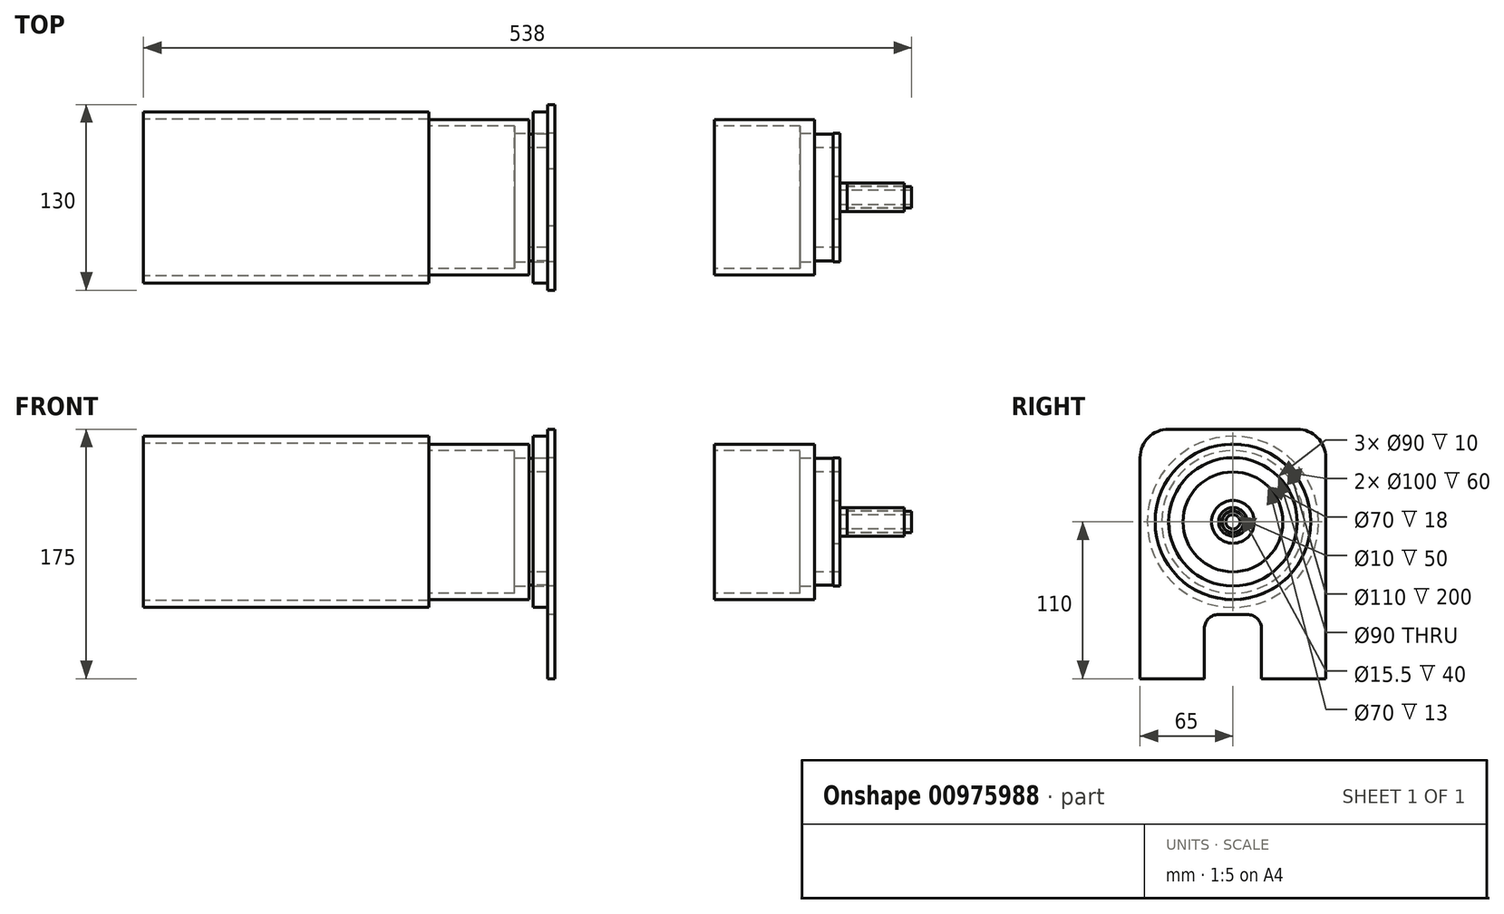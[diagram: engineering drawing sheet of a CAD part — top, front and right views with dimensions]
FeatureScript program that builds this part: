
annotation { "Feature Type Name" : "Feature", "Feature Type Description" : "" }
export const myFeature = defineFeature(function(context is Context, id is Id, definition is map)
    precondition{}
    {
        {
            var Q0;
            Q0=qCreatedBy(makeId("Right.planeOp"),FACE);
            var sketch = newSketch(context, id + "F0", { "sketchPlane" : qUnion([Q0])});
            skCircle(sketch, "E0", {"center": v(0, 0) * mm, "radius": 60 * mm});
            skCircle(sketch, "E1", {"center": v(0, 0) * mm, "radius": 55 * mm});
            skSolve(sketch);
        }
        {
            var Q0;
            Q0 = qSketchRegion(id + "F0", true);
            extrude(context, id + "F1", {"entities" : qUnion([Q0]), "depth" : 200 * mm, "offsetDistance" : 25 * mm});
        }
        {
            var Q0;
            Q0=makeQuery(id+"F1.opExtrude","CAP_FACE",FACE,{"disambiguationData":[OSD([sQuery(id+"F0.wireOp",EDGE,"E0"),sQuery(id+"F0.wireOp",EDGE,"E1")])],"isStart":false});
            var sketch = newSketch(context, id + "F2", { "sketchPlane" : qUnion([Q0])});
            skCircle(sketch, "E2", {"center": v(0, 0) * mm, "radius": 54.5 * mm});
            skCircle(sketch, "E3", {"center": v(0, 0) * mm, "radius": 50 * mm});
            skSolve(sketch);
        }
        {
            var Q0;
            Q0 = qSketchRegion(id + "F2", true);
            extrude(context, id + "F3", {"entities" : qUnion([Q0]), "depth" : 70 * mm, "offsetDistance" : 25 * mm});
        }
        {
            var Q0;
            Q0=makeQuery(id+"F3.opExtrude","CAP_FACE",FACE,{"disambiguationData":[OSD([sQuery(id+"F2.wireOp",EDGE,"E2"),sQuery(id+"F2.wireOp",EDGE,"E3")])],"isStart":false});
            var sketch = newSketch(context, id + "F4", { "sketchPlane" : qUnion([Q0])});
            skCircle(sketch, "E4", {"center": v(0, 0) * mm, "radius": 50.5 * mm});
            skCircle(sketch, "E5", {"center": v(0, 0) * mm, "radius": 45 * mm});
            skSolve(sketch);
        }
        {
            var Q0;
            Q0=makeQuery(id+"F4.imprint","IMPRINT",FACE,{"disambiguationData":[TD([[makeQuery(id+"F4.imprint","IMPRINT",EDGE,{"derivedFrom":sQuery(id+"F4.wireOp",EDGE,"E5")}),-1.0]])]});
            extrude(context, id + "F5", {"entities" : qUnion([Q0]), "operationType" : NewBodyOperationType.ADD, "oppositeDirection" : true, "depth" : 10 * mm, "offsetDistance" : 25 * mm});
        }
        {
            var Q0;
            {var subQ0=sQuery(id+"F2.wireOp",EDGE,"E3");Q0=makeQuery(id+"F5.boolean.opBoolean","MERGE",FACE,{"derivedFrom":[makeQuery(id+"F3.opExtrude","CAP_FACE",FACE,{"disambiguationData":[OSD([sQuery(id+"F2.wireOp",EDGE,"E2"),subQ0])],"isStart":false}),makeQuery(id+"F5.opExtrude","CAP_FACE",FACE,{"disambiguationData":[OSD([subQ0,sQuery(id+"F4.wireOp",EDGE,"E5")])],"isStart":true})]});}
            var sketch = newSketch(context, id + "F6", { "sketchPlane" : qUnion([Q0])});
            skCircle(sketch, "E6", {"center": v(0, 0) * mm, "radius": 44.5 * mm});
            skCircle(sketch, "E7", {"center": v(0, 0) * mm, "radius": 35 * mm});
            skSolve(sketch);
        }
        {
            var Q0;
            Q0=makeQuery(id+"F6.imprint","IMPRINT",FACE,{"disambiguationData":[TD([[makeQuery(id+"F6.imprint","IMPRINT",EDGE,{"derivedFrom":sQuery(id+"F6.wireOp",EDGE,"E6")}),1.0]])]});
            extrude(context, id + "F7", {"entities" : qUnion([Q0]), "depth" : 13 * mm, "offsetDistance" : 25 * mm});
        }
        {
            var Q0;
            Q0=makeQuery(id+"F7.opExtrude","CAP_FACE",FACE,{"disambiguationData":[OSD([sQuery(id+"F6.wireOp",EDGE,"E6"),sQuery(id+"F6.wireOp",EDGE,"E7")])],"isStart":false});
            var sketch = newSketch(context, id + "F8", { "sketchPlane" : qUnion([Q0])});
            skCircle(sketch, "E8", {"center": v(0, 0) * mm, "radius": 45 * mm});
            skCircle(sketch, "E9", {"center": v(0, 0) * mm, "radius": 60 * mm});
            skSolve(sketch);
        }
        {
            var Q0;
            Q0=makeQuery(id+"F8.imprint","IMPRINT",FACE,{"disambiguationData":[TD([[makeQuery(id+"F8.imprint","IMPRINT",EDGE,{"derivedFrom":sQuery(id+"F8.wireOp",EDGE,"E8")}),-1.0]])]});
            extrude(context, id + "F9", {"entities" : qUnion([Q0]), "oppositeDirection" : true, "depth" : 10 * mm, "offsetDistance" : 25 * mm});
        }
        {
            var Q0;
            Q0=makeQuery(id+"F9.opExtrude","CAP_FACE",FACE,{"disambiguationData":[OSD([sQuery(id+"F8.wireOp",EDGE,"E8"),sQuery(id+"F8.wireOp",EDGE,"E9")])],"isStart":true});
            var sketch = newSketch(context, id + "F10", { "sketchPlane" : qUnion([Q0])});
            skCircle(sketch, "E10", {"center": v(0, 0) * mm, "radius": 45 * mm});
            skLineSegment(sketch, "E11.bottom", {"start": v(-65, 65) * mm, "end": v(65, 65) * mm});
            skLineSegment(sketch, "E11.top", {"start": v(-65, -65) * mm, "end": v(65, -65) * mm});
            skLineSegment(sketch, "E11.left", {"start": v(-65, 65) * mm, "end": v(-65, -65) * mm});
            skLineSegment(sketch, "E11.right", {"start": v(65, 65) * mm, "end": v(65, -65) * mm});
            skLineSegment(sketch, "E12", {"start": v(65, 0) * mm, "end": v(-65, 0) * mm, "construction": true});
            skLineSegment(sketch, "E13.bottom", {"start": v(-65, -65) * mm, "end": v(-20, -65) * mm});
            skLineSegment(sketch, "E13.top", {"start": v(-65, -110) * mm, "end": v(-20, -110) * mm});
            skLineSegment(sketch, "E13.left", {"start": v(-65, -65) * mm, "end": v(-65, -110) * mm});
            skLineSegment(sketch, "E13.right", {"start": v(-20, -65) * mm, "end": v(-20, -110) * mm});
            skLineSegment(sketch, "E14.bottom", {"start": v(65, -65) * mm, "end": v(20, -65) * mm});
            skLineSegment(sketch, "E14.top", {"start": v(65, -110) * mm, "end": v(20, -110) * mm});
            skLineSegment(sketch, "E14.left", {"start": v(65, -65) * mm, "end": v(65, -110) * mm});
            skLineSegment(sketch, "E14.right", {"start": v(20, -65) * mm, "end": v(20, -110) * mm});
            skSolve(sketch);
        }
        {
            var Q0;
            Q0 = qSketchRegion(id + "F10", true);
            extrude(context, id + "F11", {"entities" : qUnion([Q0]), "depth" : 5 * mm, "offsetDistance" : 25 * mm});
        }
        {
            var Q0;
            Q0=makeQuery(id+"F11.opExtrude","SWEPT_EDGE",EDGE,{"disambiguationData":[OSD([sQuery(id+"F10.wireOp",EDGE,"E11.bottom"),sQuery(id+"F10.wireOp",EDGE,"E11.left")])]});
            var Q1;
            Q1=makeQuery(id+"F11.opExtrude","SWEPT_EDGE",EDGE,{"disambiguationData":[OSD([sQuery(id+"F10.wireOp",EDGE,"E11.bottom"),sQuery(id+"F10.wireOp",EDGE,"E11.right")])]});
            fillet(context, id + "F12", {"entities" : qUnion([Q0, Q1]), "radius" : 20 * mm, "tangentPropagation" : true, "allowEdgeOverflow" : false});
        }
        {
            var Q0;
            Q0=makeQuery(id+"F11.opExtrude","SWEPT_EDGE",EDGE,{"disambiguationData":[OSD([sQuery(id+"F10.wireOp",EDGE,"E11.top"),sQuery(id+"F10.wireOp",EDGE,"E13.bottom"),sQuery(id+"F10.wireOp",EDGE,"E13.right")])]});
            var Q1;
            Q1=makeQuery(id+"F11.opExtrude","SWEPT_EDGE",EDGE,{"disambiguationData":[OSD([sQuery(id+"F10.wireOp",EDGE,"E11.top"),sQuery(id+"F10.wireOp",EDGE,"E14.bottom"),sQuery(id+"F10.wireOp",EDGE,"E14.right")])]});
            fillet(context, id + "F13", {"entities" : qUnion([Q0, Q1]), "radius" : 10 * mm, "tangentPropagation" : true, "allowEdgeOverflow" : false});
        }
        {
            var Q0;
            Q0=makeQuery(id+"F3.opExtrude","SWEPT_BODY",BODY,{"disambiguationData":[OSD([sQuery(id+"F2.wireOp",EDGE,"E2"),sQuery(id+"F2.wireOp",EDGE,"E3")])]});
            transform(context, id + "F14", {"entities" : qUnion([Q0]), "transformType" : TransformType.TRANSLATION_3D, "dx" : 200 * mm, "dy" : 0 * mm, "dz" : 0 * mm, "makeCopy" : true});
        }
        {
            var Q0;
            Q0=makeQuery(id+"F7.opExtrude","SWEPT_BODY",BODY,{"disambiguationData":[OSD([sQuery(id+"F6.wireOp",EDGE,"E6"),sQuery(id+"F6.wireOp",EDGE,"E7")])]});
            transform(context, id + "F15", {"entities" : qUnion([Q0]), "transformType" : TransformType.TRANSLATION_3D, "dx" : 200 * mm, "dy" : 0 * mm, "dz" : 0 * mm, "makeCopy" : true});
        }
        {
            var Q0;
            Q0=makeQuery(id+"F15.opPattern","COPY",FACE,{"derivedFrom":makeQuery(id+"F7.opExtrude","CAP_FACE",FACE,{"disambiguationData":[OSD([sQuery(id+"F6.wireOp",EDGE,"E6"),sQuery(id+"F6.wireOp",EDGE,"E7")])],"isStart":false}),"instanceName":"1"});
            var sketch = newSketch(context, id + "F16", { "sketchPlane" : qUnion([Q0])});
            skCircle(sketch, "E15", {"center": v(0, 0) * mm, "radius": 35 * mm});
            skCircle(sketch, "E16", {"center": v(0, 0) * mm, "radius": 32.5 * mm});
            skSolve(sketch);
        }
        {
            var Q0;
            Q0 = qSketchRegion(id + "F16", true);
            extrude(context, id + "F17", {"entities" : qUnion([Q0]), "oppositeDirection" : true, "depth" : 5 * mm, "offsetDistance" : 25 * mm});
        }
        {
            var Q0;
            Q0=makeQuery(id+"F17.opExtrude","CAP_FACE",FACE,{"disambiguationData":[OSD([sQuery(id+"F16.wireOp",EDGE,"E15"),sQuery(id+"F16.wireOp",EDGE,"E16")])],"isStart":true});
            var sketch = newSketch(context, id + "F18", { "sketchPlane" : qUnion([Q0])});
            skCircle(sketch, "E17", {"center": v(0, 0) * mm, "radius": 45 * mm});
            skSolve(sketch);
        }
        {
            var Q0;
            Q0 = qSketchRegion(id + "F18", true);
            extrude(context, id + "F19", {"entities" : qUnion([Q0]), "operationType" : NewBodyOperationType.ADD, "depth" : 5 * mm, "offsetDistance" : 25 * mm});
        }
        {
            var Q0;
            Q0=makeQuery(id+"F19.opExtrude","CAP_FACE",FACE,{"disambiguationData":[OSD([sQuery(id+"F18.wireOp",EDGE,"E17")])],"isStart":false});
            var sketch = newSketch(context, id + "F20", { "sketchPlane" : qUnion([Q0])});
            skCircle(sketch, "E18", {"center": v(0, 0) * mm, "radius": 35 * mm});
            skCircle(sketch, "E19", {"center": v(0, 0) * mm, "radius": 15 * mm});
            skSolve(sketch);
        }
        {
            var Q0;
            Q0=makeQuery(id+"F20.imprint","IMPRINT",FACE,{"disambiguationData":[TD([[makeQuery(id+"F20.imprint","IMPRINT",EDGE,{"derivedFrom":sQuery(id+"F20.wireOp",EDGE,"E18")}),1.0]])]});
            extrude(context, id + "F21", {"entities" : qUnion([Q0]), "operationType" : NewBodyOperationType.REMOVE, "endBound" : BoundingType.UP_TO_NEXT, "oppositeDirection" : true, "depth" : 25 * mm, "offsetDistance" : 25 * mm});
        }
        {
            var Q0;
            Q0=makeQuery(id+"F21.boolean.opBoolean","SPLIT",FACE,{"disambiguationData":[TD([makeQuery(id+"F21.opExtrude","SWEPT_FACE",FACE,{"disambiguationData":[OSD([sQuery(id+"F20.wireOp",EDGE,"E19")])]})])],"derivedFrom":makeQuery(id+"F19.opExtrude","CAP_FACE",FACE,{"disambiguationData":[OSD([sQuery(id+"F18.wireOp",EDGE,"E17")])],"isStart":false})});
            var sketch = newSketch(context, id + "F22", { "sketchPlane" : qUnion([Q0])});
            skCircle(sketch, "E20", {"center": v(0, 0) * mm, "radius": 7.5 * mm});
            skCircle(sketch, "E21", {"center": v(0, 0) * mm, "radius": 5 * mm});
            skCircle(sketch, "E22", {"center": v(0, 0) * mm, "radius": 10 * mm});
            skSolve(sketch);
        }
        {
            var Q0;
            Q0=makeQuery(id+"F22.imprint","IMPRINT",FACE,{"disambiguationData":[TD([[makeQuery(id+"F22.imprint","IMPRINT",EDGE,{"derivedFrom":sQuery(id+"F22.wireOp",EDGE,"E20")}),1.0]])]});
            extrude(context, id + "F23", {"entities" : qUnion([Q0]), "operationType" : NewBodyOperationType.ADD, "depth" : 50 * mm, "offsetDistance" : 25 * mm});
        }
        {
            var Q0;
            Q0 = qSketchRegion(id + "F22", true);
            extrude(context, id + "F24", {"entities" : qUnion([Q0]), "operationType" : NewBodyOperationType.ADD, "depth" : 5 * mm, "offsetDistance" : 25 * mm});
        }
        {
            var Q0;
            Q0=makeQuery(id+"F24.opExtrude","CAP_FACE",FACE,{"disambiguationData":[OSD([sQuery(id+"F22.wireOp",EDGE,"E20"),sQuery(id+"F22.wireOp",EDGE,"E22")])],"isStart":false});
            var sketch = newSketch(context, id + "F25", { "sketchPlane" : qUnion([Q0])});
            skCircle(sketch, "E23", {"center": v(0, 0) * mm, "radius": 7.75 * mm});
            skCircle(sketch, "E24", {"center": v(0, 0) * mm, "radius": 10 * mm});
            skLineSegment(sketch, "E25", {"start": v(0, 0) * mm, "end": v(0, 10) * mm, "construction": true});
            skLineSegment(sketch, "E26.bottom", {"start": v(-2.13, 90) * mm, "end": v(2.13, 90) * mm});
            skLineSegment(sketch, "E26.top", {"start": v(-2.13, 10) * mm, "end": v(2.13, 10) * mm});
            skPoint(sketch, "E26.middle", {"position": v(0, 50) * mm});
            skLineSegment(sketch, "E27", {"start": v(-2.13, 90) * mm, "end": v(-2.13, 10) * mm});
            skLineSegment(sketch, "E28", {"start": v(-2.13, 90) * mm, "end": v(-2.13, 9.77) * mm, "construction": true});
            skLineSegment(sketch, "E29", {"start": v(2.13, 90) * mm, "end": v(2.13, 9.77) * mm, "construction": true});
            skSolve(sketch);
        }
        {
            var Q0;
            Q0 = qSketchRegion(id + "F25", true);
            extrude(context, id + "F26", {"entities" : qUnion([Q0]), "depth" : 40 * mm, "offsetDistance" : 25 * mm});
        }
    });
